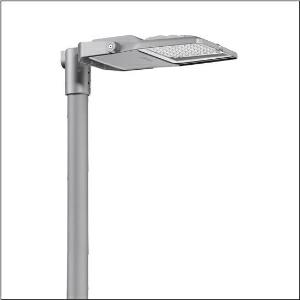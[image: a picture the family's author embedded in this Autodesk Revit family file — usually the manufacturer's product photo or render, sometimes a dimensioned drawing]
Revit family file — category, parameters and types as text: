
# Revit family: floodlight_fl_21_iq_mini___pl61_5xa7772b2c3a_0206
name_source: partatom
category: Lighting Fixtures
units: mm (PartAtom-declared; Revit-internal decimal feet)

## family parameters
Cut with Voids When Loaded = No
Host = Face
Light Source = No
Part Type = Normal
Room Calculation Point = No
Round Connector Dimension = Use Diameter
Shared = No

## types (1)
- --- (1 x LED, 6120 lm, 45.5 W, 3000K)
    Apparent Load = 46 VA
    CIE Flux Codes = 33 65 98 100 100
    Color Rendering = 70
    Color Temperature = 3000K
    Default Elevation = 1800 mm
    Description = Floodlight FL 21 iQ mini, floodlight, primary light control with lens, of PMMA, primary optical cover: protective disc, of toughened safety glass, transparent, light distribution: PL61, light emission: direct distribution, installation type: surface-mounted, LED, High Power LED, rated luminous flux: 6.120lm, luminous efficacy: 135lm/W, light colour: 730, colour temperature: 3000K, control: Auto-Match, Temp-Guard, Night-Set, Smart-Wire, Desk-Remote (wireless, voltage-free reading and setting of iQ features in the workshop via application-optimized NFC function/RFID function), optimised constant luminous flux control (CLO 2.0), Light-Fading, Lumen-Switch, with terminal, 6-pole, mains connection: 220..240V, AC, 50/60Hz, start of lifetime: 46W, end of service life: 48W, reduction: 22W, luminaire housing, of diecast aluminium, powder-coated, Siteco® metallic grey (DB 702S), corrosivity category C5 mid according to DIN EN ISO 12944, sealing non-destructively replaceable, please order mast flange separately, mast bracket, of steel, galvanised, powder-coated, protection rating (complete): IP66, insulation class (complete): insulation class II (safety insulation), certification: CE, ENEC, VDE, protection symbol: D, impact resistance: IK08, permissible operating ambient temperature: -40..+40°C, permissible operating ambient temperature for outdoor applications: -40..+50°C, standard: DIN EN 12944, LABS conformity tested according to VDMA 24364:2018-05, packaging unit: 1 piece

Light Distribution: PL61
    Height = 70 mm
    Lamp = 1 x LED
    Lamp Light Flux = 6120 lm
    Lamp Power = 45.5 W
    Lamp count = 1
    Length = 485 mm
    Luminous efficacy = 135 lm/W
    Manufacturer = Siteco
    ModVariant = No
    Model = 5XA7772B2C3A
    Number of Poles = 1
    OnlyDefault = Yes
    Power Factor = 1
    Product Name = Floodlight FL 21 iQ mini | PL61
    Product group = floodlight | pylon annexe
    ProductGroupID = 6200
    Protection Class = Protection class II
    Protection Degree = IP 66
    RLX_Detail_Level = 1
    RLX_Emergency_Light_Flux = 0 lm
    RLX_Emergency_Type = 0
    RLX_Emergency_Type_DB = No
    RlxData = <blob elided: 101301 chars, md5=75a3998a>
    Socket = socket
    Standby Power = 0 W
    System Light Flux = 6120 lm
    System Power = 46 W
    Type Comments = factory setting: luminous flux: 100 % | dim-lin: 254 | 463 mA
    Type Image = l_1007125.jpg
    URL = http://relux.com
    VarID = @adj_144693
    Voltage = 0 V
    Weight = 0.00 kg
    Width = 337 mm

## geometry (parser evidence)
native form markers: Blend x4, Sweep x13
no freeform markers — native parametric forms only
